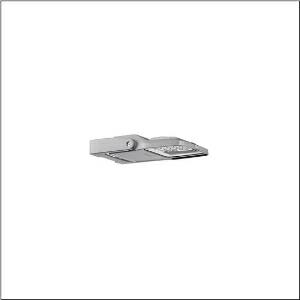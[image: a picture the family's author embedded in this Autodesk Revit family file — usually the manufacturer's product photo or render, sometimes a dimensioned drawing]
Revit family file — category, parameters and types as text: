
# Revit family: floodlight_fl_21_iq_micro___pl61_5xa7762a2c2a_d8df
name_source: partatom
category: Lighting Fixtures
units: mm (PartAtom-declared; Revit-internal decimal feet)

## family parameters
Cut with Voids When Loaded = No
Host = Face
Light Source = No
Part Type = Normal
Room Calculation Point = No
Round Connector Dimension = Use Diameter
Shared = No

## types (1)
- --- (1 x LED, 2910 lm, 23.1 W, 3000K)
    Apparent Load = 23 VA
    CIE Flux Codes = 33 65 98 100 100
    Color Rendering = 70
    Color Temperature = 3000K
    Default Elevation = 1800 mm
    Description = Floodlight FL 21 iQ micro, floodlight, primary light control with lens, of PMMA, primary optical cover: protective disc, of toughened safety glass, transparent, light distribution: PL61, light emission: direct distribution, installation type: surface-mounted, LED, High Power LED, rated luminous flux: 2.910lm, luminous efficacy: 126lm/W, light colour: 730, colour temperature: 3000K, control gear: iQ Street-Remote/DALI, control: Auto-Match, Temp-Guard, Night-Set, Smart-Wire, Desk-Remote (wireless, voltage-free reading and setting of iQ features in the workshop via application-optimized NFC function/RFID function), optimised constant luminous flux control (CLO 2.0), Street-Remote, with terminal, 6-pole, mains connection: 220..240V, AC, 50/60Hz, start of lifetime: 23W, end of service life: 24W, reduction: 11W, luminaire housing, of diecast aluminium, powder-coated, Siteco® metallic grey (DB 702S), corrosivity category C5 mid according to DIN EN ISO 12944, suitable for swimming pools, chlorine-resistant, sealing non-destructively replaceable, design bracket, of diecast aluminium, powder-coated, Siteco® metallic grey (DB 702S), protection rating (complete): IP66, insulation class (complete): insulation class II (safety insulation), certification: CE, ENEC, VDE, protection symbol: D, impact resistance: IK07, permissible operating ambient temperature: -40..+40°C, permissible operating ambient temperature for outdoor applications: -40..+50°C, standard: DIN EN 12944, LABS conformity tested according to VDMA 24364:2018-05, packaging unit: 1 piece

Light Distribution: PL61
    Height = 65 mm
    Lamp = 1 x LED
    Lamp Light Flux = 2910 lm
    Lamp Power = 23.1 W
    Lamp count = 1
    Length = 312 mm
    Luminous efficacy = 126 lm/W
    Manufacturer = Siteco
    ModVariant = No
    Model = 5XA7762A2C2A
    Mounting Place = Wall
    Mounting Type = Surface mounted
    Number of Poles = 1
    OnlyDefault = Yes
    Power Factor = 1
    Product Name = Floodlight FL 21 iQ micro | PL61
    Product group = floodlight | wall mounted
    ProductGroupID = 2001
    Protection Class = Protection class II
    Protection Degree = IP 66
    RLX_Detail_Level = 1
    RLX_Emergency_Light_Flux = 0 lm
    RLX_Emergency_Type = 0
    RLX_Emergency_Type_DB = No
    RlxData = <blob elided: 97549 chars, md5=0f260533>
    Socket = socket
    Standby Power = 0 W
    System Light Flux = 2910 lm
    System Power = 23 W
    Type Comments = factory setting: luminous flux: 100 % | dim-lin: 254 | 455 mA
    Type Image = l_1006878.jpg
    URL = http://relux.com
    VarID = @adj_194404
    Voltage = 0 V
    Weight = 0.00 kg
    Width = 230 mm

## geometry (parser evidence)
native form markers: Blend x4, Sweep x13
no freeform markers — native parametric forms only
